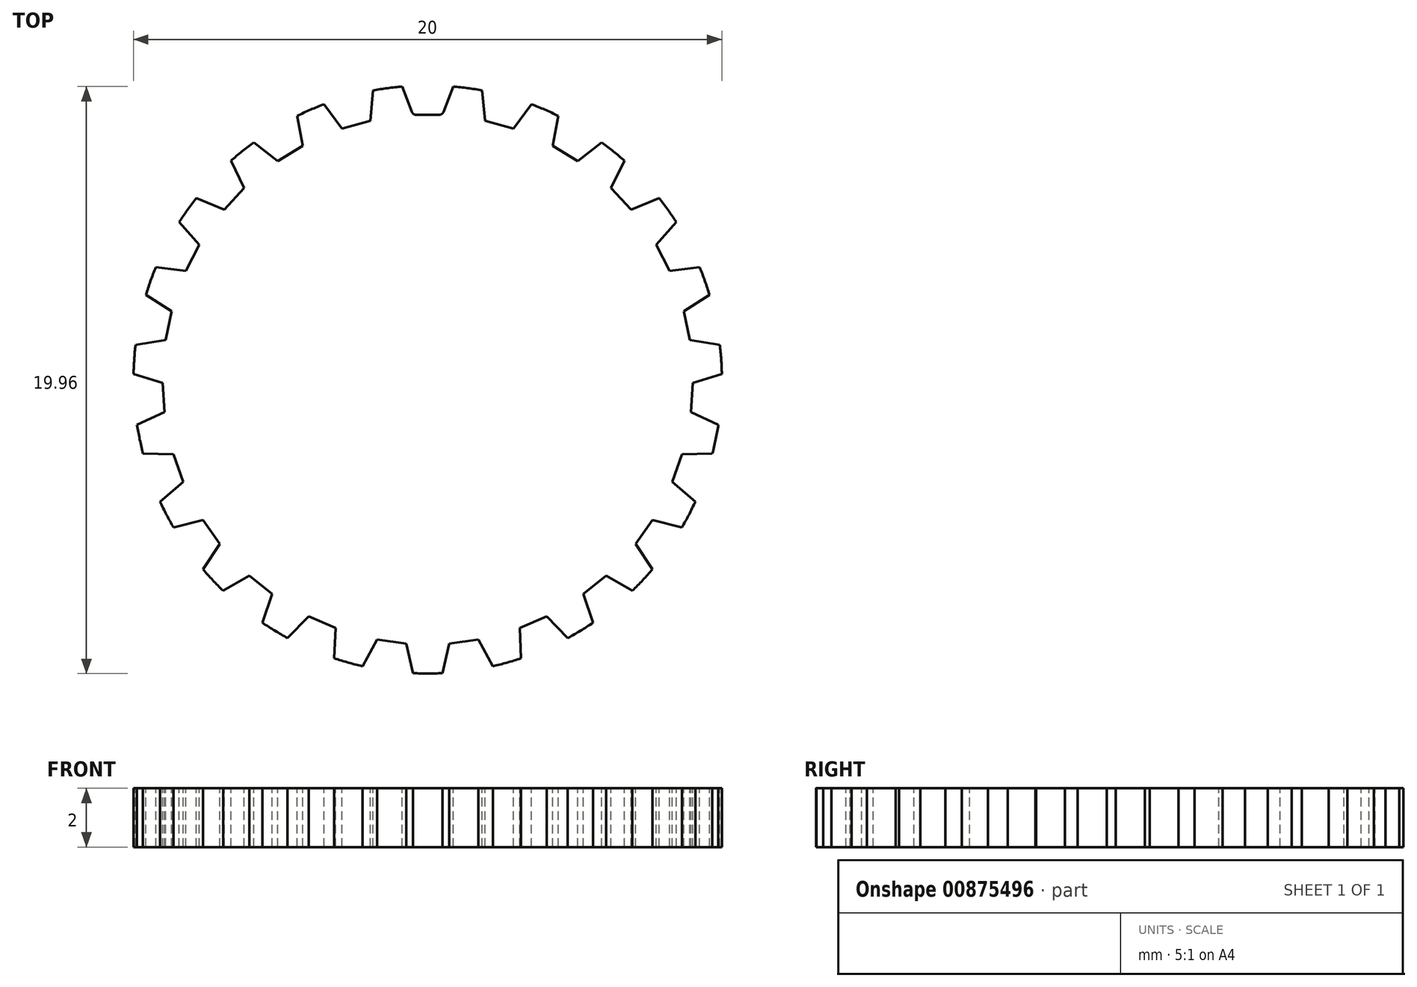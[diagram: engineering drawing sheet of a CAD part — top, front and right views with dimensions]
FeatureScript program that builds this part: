
annotation { "Feature Type Name" : "Feature", "Feature Type Description" : "" }
export const myFeature = defineFeature(function(context is Context, id is Id, definition is map)
    precondition{}
    {
        {
            var Q0;
            Q0=qCreatedBy(makeId("Top.planeOp"),FACE);
            var sketch = newSketch(context, id + "F0", { "sketchPlane" : qUnion([Q0])});
            skCircle(sketch, "E0", {"center": v(0, 0) * mm, "radius": 10 * mm});
            skSolve(sketch);
        }
        {
            var Q0;
            Q0=qSketchRegion(id+"F0",true);
            extrude(context, id + "F1", {"entities" : qUnion([Q0]), "depth" : 2 * mm, "offsetDistance" : 25 * mm});
        }
        {
            var Q0;
            Q0=makeQuery(id+"F1.opExtrude","CAP_FACE",FACE,{"disambiguationData":[OSD([sQuery(id+"F0.wireOp",EDGE,"E0")])],"isStart":false});
            var sketch = newSketch(context, id + "F2", { "sketchPlane" : qUnion([Q0])});
            skLineSegment(sketch, "E1", {"start": v(0, 0) * mm, "end": v(0, 9) * mm});
            skLineSegment(sketch, "E2", {"start": v(0, 9) * mm, "end": v(0.5, 9) * mm});
            skLineSegment(sketch, "E3", {"start": v(0, 9) * mm, "end": v(0, 10) * mm});
            skLineSegment(sketch, "E4", {"start": v(0, 10) * mm, "end": v(0.88, 10) * mm});
            skLineSegment(sketch, "E5", {"start": v(0.88, 10) * mm, "end": v(0.5, 9) * mm});
            skLineSegment(sketch, "E6.MirrorCS", {"start": v(0, 10) * mm, "end": v(-0.88, 10) * mm});
            skLineSegment(sketch, "E7.MirrorCS", {"start": v(-0.88, 10) * mm, "end": v(-0.5, 9) * mm});
            skLineSegment(sketch, "E8.MirrorCS", {"start": v(0, 9) * mm, "end": v(-0.5, 9) * mm});
            skSolve(sketch);
        }
        {
            var Q0;
            {var subQ0=sQuery(id+"F2.wireOp",EDGE,"E2");Q0=makeQuery(id+"F2.imprint","IMPRINT",FACE,{"disambiguationData":[TD([[makeQuery(id+"F2.imprint","IMPRINT",EDGE,{"derivedFrom":subQ0}),1.0]])]});}
            var Q1;
            {var subQ0=sQuery(id+"F2.wireOp",EDGE,"E3");Q1=makeQuery(id+"F2.imprint","IMPRINT",FACE,{"disambiguationData":[TD([[makeQuery(id+"F2.imprint","IMPRINT",EDGE,{"derivedFrom":subQ0}),1.0]])]});}
            extrude(context, id + "F3", {"entities" : qUnion([Q0, Q1]), "operationType" : NewBodyOperationType.REMOVE, "oppositeDirection" : true, "depth" : 25 * mm, "offsetDistance" : 25 * mm});
        }
        {
            var Q0;
            Q0=makeQuery(id+"F3.boolean.opBoolean","COPY",FACE,{"derivedFrom":makeQuery(id+"F3.opExtrude","SWEPT_FACE",FACE,{"disambiguationData":[OSD([sQuery(id+"F2.wireOp",EDGE,"E5")])]})});
            var Q1;
            Q1=makeQuery(id+"F3.boolean.opBoolean","COPY",FACE,{"derivedFrom":makeQuery(id+"F3.opExtrude","SWEPT_FACE",FACE,{"disambiguationData":[OSD([sQuery(id+"F2.wireOp",EDGE,"E2"),sQuery(id+"F2.wireOp",EDGE,"E8.MirrorCS")])]})});
            var Q2;
            Q2=makeQuery(id+"F3.boolean.opBoolean","COPY",FACE,{"derivedFrom":makeQuery(id+"F3.opExtrude","SWEPT_FACE",FACE,{"disambiguationData":[OSD([sQuery(id+"F2.wireOp",EDGE,"E7.MirrorCS")])]})});
            var Q3;
            Q3=makeQuery(id+"F1.opExtrude","SWEPT_FACE",FACE,{"disambiguationData":[OSD([sQuery(id+"F0.wireOp",EDGE,"E0")])]});
            circularPattern(context, id + "F4", {"patternType" : PatternType.FACE, "faces" : qUnion([Q0, Q1, Q2]), "axis" : qUnion([Q3]), "angle" : 360 * degree, "instanceCount" : 23, "equalSpace" : true});
        }
        {
            var Q0;
            Q0=makeQuery(id+"F3.boolean.opBoolean","COPY",EDGE,{"derivedFrom":makeQuery(id+"F3.opExtrude","SWEPT_EDGE",EDGE,{"disambiguationData":[OSD([sQuery(id+"F2.wireOp",EDGE,"E2"),sQuery(id+"F2.wireOp",EDGE,"E5")])]})});
            var Q1;
            Q1=makeQuery(id+"F3.boolean.opBoolean","COPY",EDGE,{"derivedFrom":makeQuery(id+"F3.opExtrude","SWEPT_EDGE",EDGE,{"disambiguationData":[OSD([sQuery(id+"F2.wireOp",EDGE,"E7.MirrorCS"),sQuery(id+"F2.wireOp",EDGE,"E8.MirrorCS")])]})});
            var Q2;
            Q2=makeQuery(id+"F3.boolean.opBoolean","COPY",EDGE,{"derivedFrom":makeQuery(id+"F3.opExtrude","SWEPT_EDGE",EDGE,{"disambiguationData":[OSD([sQuery(id+"F0.wireOp",EDGE,"E0"),sQuery(id+"F2.wireOp",EDGE,"E5")])]})});
            var Q3;
            Q3=makeQuery(id+"F3.boolean.opBoolean","COPY",EDGE,{"derivedFrom":makeQuery(id+"F3.opExtrude","SWEPT_EDGE",EDGE,{"disambiguationData":[OSD([sQuery(id+"F0.wireOp",EDGE,"E0"),sQuery(id+"F2.wireOp",EDGE,"E7.MirrorCS")])]})});
            fillet(context, id + "F5", {"entities" : qUnion([Q0, Q1, Q2, Q3]), "radius" : .15 * mm, "tangentPropagation" : true, "allowEdgeOverflow" : false});
        }
    });
